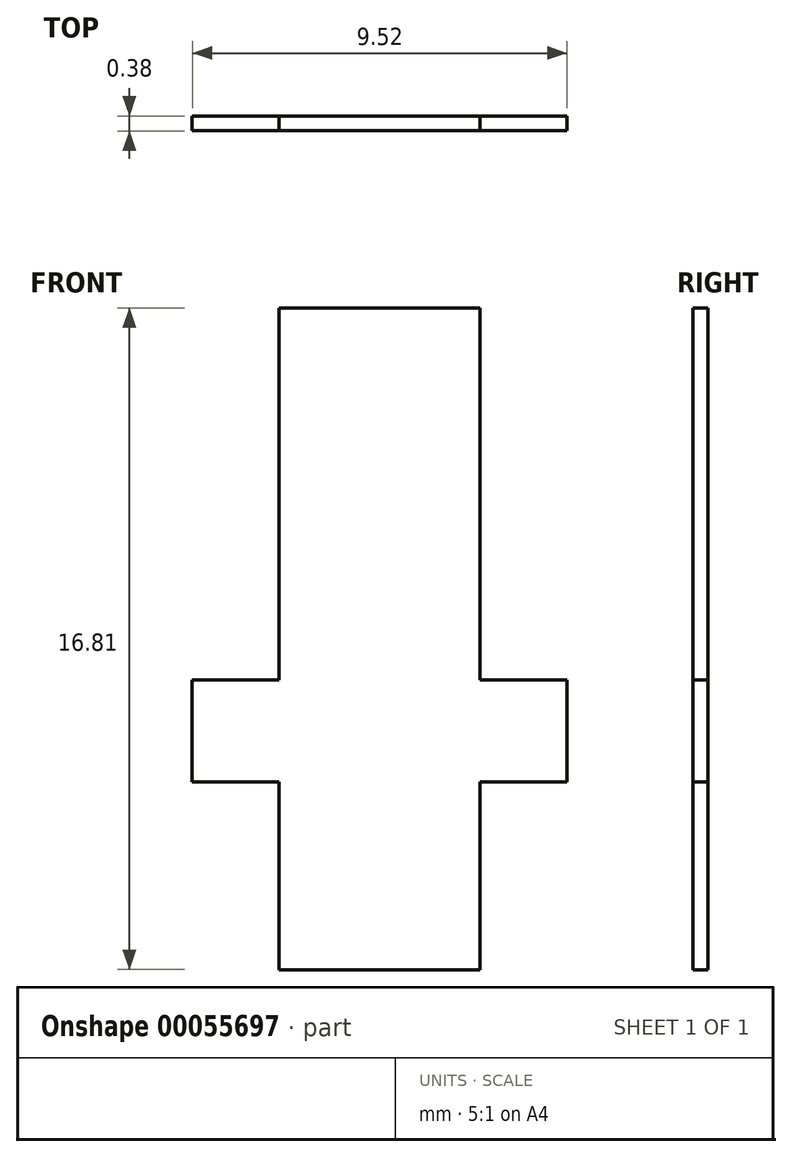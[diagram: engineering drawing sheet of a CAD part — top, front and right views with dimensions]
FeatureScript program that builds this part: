
annotation { "Feature Type Name" : "Feature", "Feature Type Description" : "" }
export const myFeature = defineFeature(function(context is Context, id is Id, definition is map)
    precondition{}
    {
        {
            assignVariable(context, id + "F0", {"name" : "thick", "anyValue" : .188});
        }
        {
            var Q0;
            Q0=qCreatedBy(makeId("Front.planeOp"),FACE);
            var sketch = newSketch(context, id + "F1", { "sketchPlane" : qUnion([Q0])});
            skLineSegment(sketch, "E0", {"start": v(-2.55, 0) * mm, "end": v(-2.55, 9.45) * mm});
            skLineSegment(sketch, "E1", {"start": v(-2.55, 9.45) * mm, "end": v(2.55, 9.45) * mm});
            skLineSegment(sketch, "E2", {"start": v(2.55, 9.45) * mm, "end": v(2.55, 0) * mm});
            skLineSegment(sketch, "E3", {"start": v(2.55, 0) * mm, "end": v(4.76, 0) * mm});
            skLineSegment(sketch, "E4", {"start": v(4.76, 0) * mm, "end": v(4.76, -2.59) * mm});
            skLineSegment(sketch, "E5", {"start": v(4.76, -2.59) * mm, "end": v(2.55, -2.59) * mm});
            skLineSegment(sketch, "E6", {"start": v(2.55, -2.59) * mm, "end": v(2.55, -7.36) * mm});
            skLineSegment(sketch, "E7", {"start": v(2.55, -7.36) * mm, "end": v(-2.55, -7.36) * mm});
            skLineSegment(sketch, "E8", {"start": v(-2.55, -7.36) * mm, "end": v(-2.55, -2.59) * mm});
            skLineSegment(sketch, "E9", {"start": v(-2.55, -2.59) * mm, "end": v(-4.76, -2.59) * mm});
            skLineSegment(sketch, "E10", {"start": v(-4.76, -2.59) * mm, "end": v(-4.76, 0) * mm});
            skLineSegment(sketch, "E11", {"start": v(-4.76, 0) * mm, "end": v(-2.55, 0) * mm});
            skLineSegment(sketch, "E12", {"start": v(-2.55, 0) * mm, "end": v(0, 0) * mm, "construction": true});
            skLineSegment(sketch, "E13", {"start": v(2.55, 0) * mm, "end": v(0, 0) * mm, "construction": true});
            skSolve(sketch);
        }
        {
            var Q0;
            Q0=qSketchRegion(id+"F1",true);
            extrude(context, id + "F2", {"entities" : qUnion([Q0]), "endBound" : BoundingType.SYMMETRIC, "depth" : (getVariable(context, 'thick') * 2) * mm});
        }
    });
